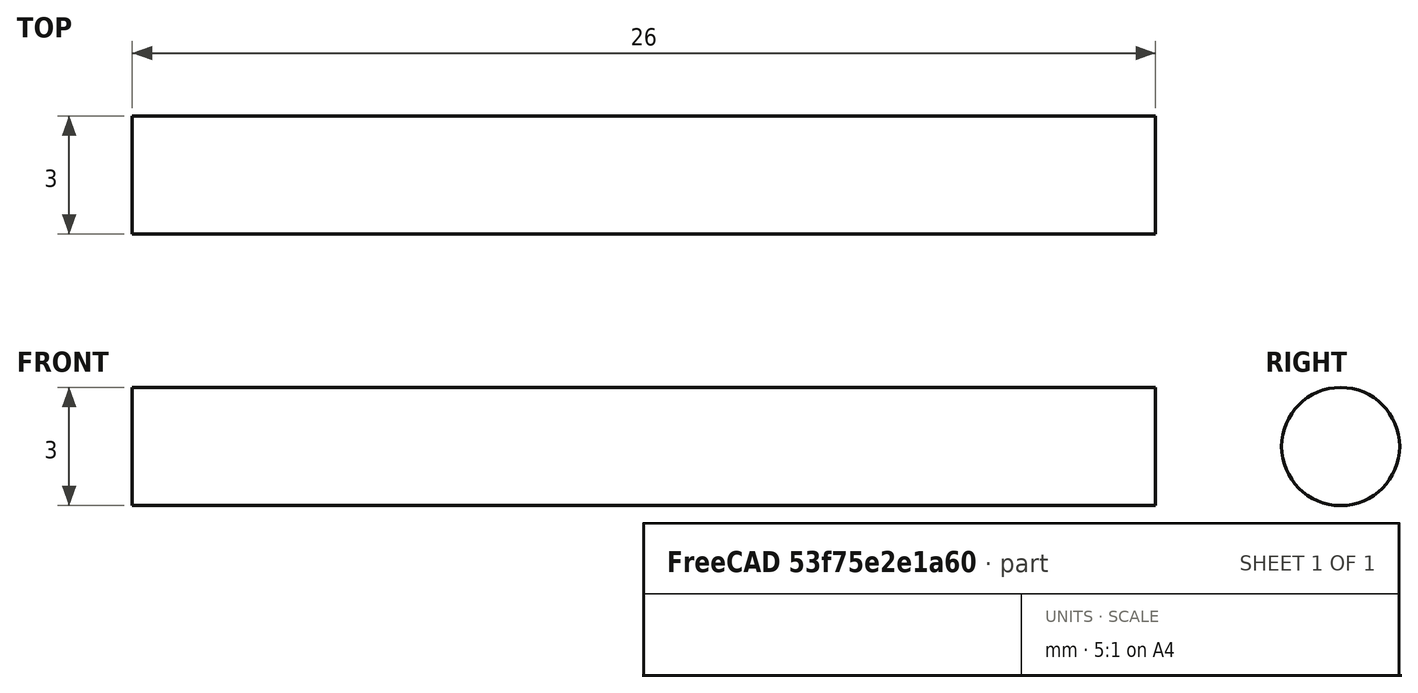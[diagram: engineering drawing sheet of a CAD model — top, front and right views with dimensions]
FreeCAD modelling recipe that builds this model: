
FCSTD DOCUMENT  (FreeCAD 0.20R)
Label: eje
License: All rights reserved
LicenseURL: http://en.wikipedia.org/wiki/All_rights_reserved
objects: Sketcher::SketchObject×1, PartDesign::Pad×1, PartDesign::Body×1
note: 4 computed .brp shape members not serialized (recipe doc carries the construction recipe); baked Part::Feature solids carry a one-line shape summary decoded from their .brp

FEATURE [Sketcher::SketchObject] Sketch
  FullyConstrained = true
  MapMode = 5
  Placement = pos=(0,0,0) rot=(0.57735,0.57735,0.57735;2.0944rad)
  Support = -> [YZ_Plane]
  sketch-geometry (1):
    g0: Circle CenterX=0 CenterY=0 CenterZ=0 NormalX=0 NormalY=0 NormalZ=1 AngleXU=0 Radius=1.5
  constraints (2):
    c: Coincident(g0,g-1)
    c: Diameter(g0) = 3
FEATURE [PartDesign::Pad] Pad
  Direction = (1,-2e-16,3e-16)
  Length = 26
  Length2 = 10
  Midplane = true
  Placement = pos=(0,0,0) rot=(0.57735,0.57735,0.57735;2.0944rad)
  Profile = -> Sketch
  ReferenceAxis = -> Sketch [N_Axis]
  Type = 0
FEATURE [PartDesign::Body] Body
  Group = -> [Sketch,Pad]
  Origin = -> Origin
  Tip = -> Pad
